# Revit family: PRE030022
name_source: partatom
category: Accessoire de canalisation
revit_build: Autodesk Revit 2015 (Build: 20140606_1530(x64)
units: mm (PartAtom-declared; Revit-internal decimal feet)

## types (2) — shared parameters
Adresse du fabricant = 7 RUE RACINE  92542 MONTROUGE CEDEX FRANCE
Corps = PRESTO Laiton
Eau chaude = PRESTO Rouge
Eau froide = PRESTO Noir
Fabricant = LES ROBINETS PRESTO SA
Finition = Laiton Chrome
Garantie = 10 ans
Hauteur nominale = -
Lien CCTP = http://www.prestodatashare.com
Lien données techniques = http://www.prestodatashare.com
Lien site internet = http://www.prestodatashare.com
Longueur nominale = -
Pertes de charge = 100.0 Pa
Pression = 1 a 5 bars Pression de service, statique maxi : 10 bars
Profondeur nominale = -
Type de raccordement = -
URL fabricant = http://www.prestodatashare.com
Variateur = PRESTO Variateur
Version = 15
zero-valued in all types: Elévation par défaut

## per-type parameters (varying)
| type | Diamètre nominal entrée | Diamètre nominal sortie | Débit | Fonction | Nom | Polantis code | Référence |
| 84020 Prestotherm XL 280L | 25 mm  [stored 0.082021 ft] | 32 mm  [stored 0.104987 ft] | Debit maximum : 280 L/Mn a 3 bars Minimum : 15 L/Mn a 3 bars | Entrees G 1" (26x34) Sortie G 1"1/4 (33x42) | 84020 Presto Mitigeur centralise prestotherm XL | PRE030022 | 84020 |
| 84021 Prestotherm XL 450L | 32 mm  [stored 0.104987 ft] | 40 mm  [stored 0.131234 ft] | Debit maximum : 450 L/Mn a 3 bars Minimum : 50 L/Mn a 3 bars | Entrees G 1"1/4 (33x42) Sortie G 1"1/2 (40x49) | 84021 Presto Mitigeur centralise prestotherm XL | PRE030022a | 84021 |

note: [stored X ft] marks values corroborated as IEEE doubles in the binary element streams (Revit-internal decimal feet)

## geometry (parser evidence)
native form markers: Blend x6, Sweep x1
no freeform markers — native parametric forms only
